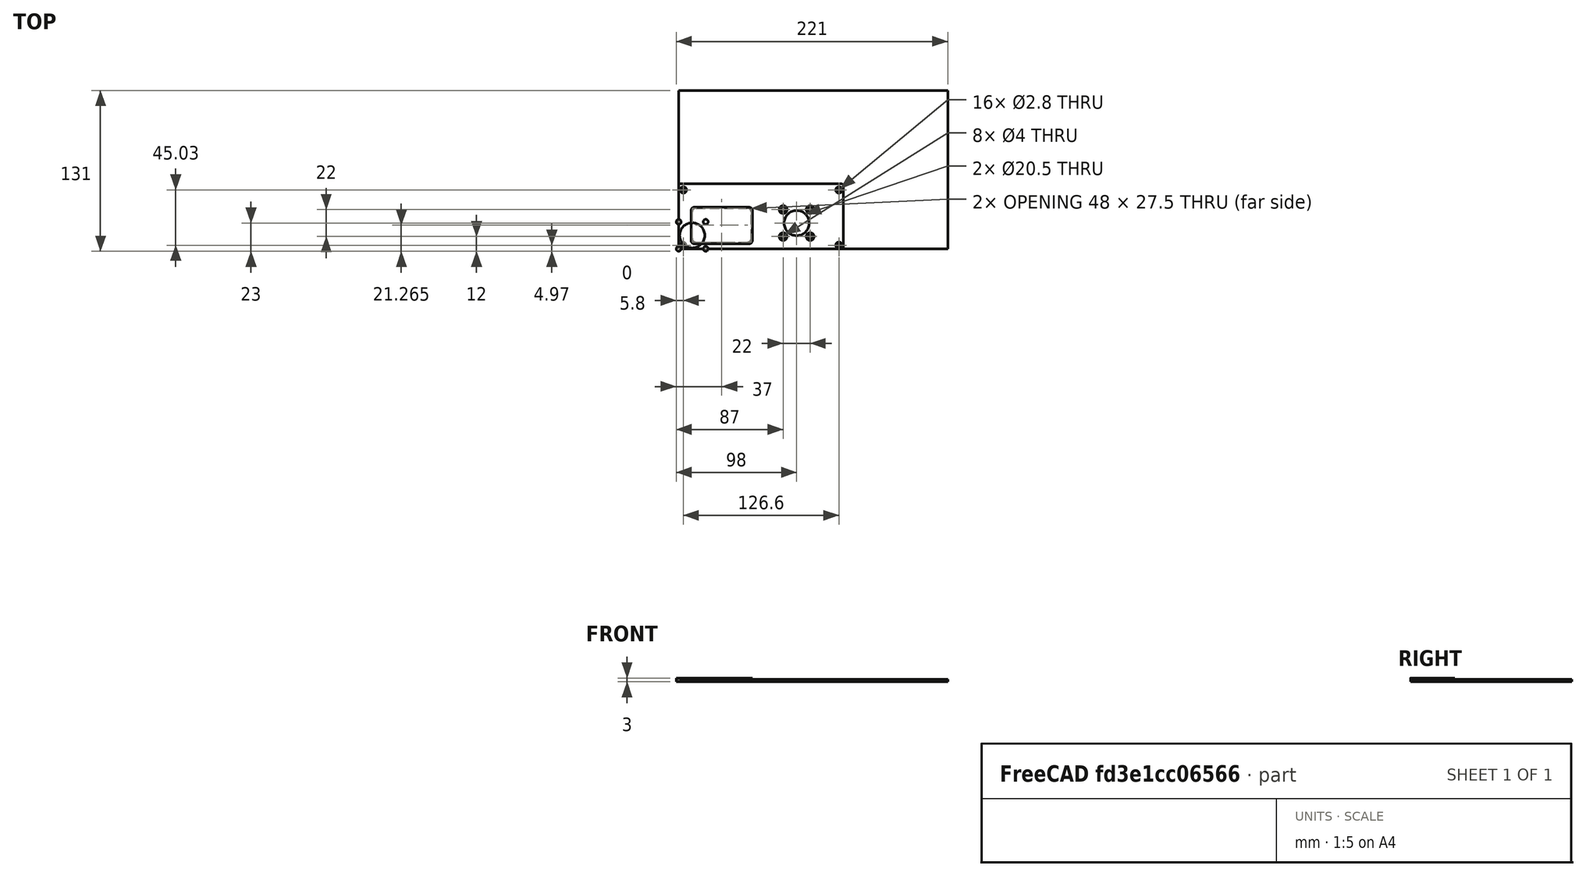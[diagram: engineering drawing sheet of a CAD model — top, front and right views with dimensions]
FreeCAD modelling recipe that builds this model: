
FCSTD DOCUMENT  (FreeCAD 0.17R13522 (Git))
Label: 温度控制器外壳dangyang
License: All rights reserved
LicenseURL: http://en.wikipedia.org/wiki/All_rights_reserved
objects: Drawing::FeatureViewPython×10, Part::Cylinder×6, Part::Feature×6, Part::Box×4, Part::Fillet×3, Part::Cut×3, Part::MultiFuse×2, Part::Chamfer×2, Part::FeaturePython×1, Raytracing::RayFeature×1, Raytracing::RayProject×1, Drawing::FeatureViewPart×1, Drawing::FeaturePage×1
note: 27 computed .brp shape members not serialized (recipe doc carries the construction recipe); baked Part::Feature solids carry a one-line shape summary decoded from their .brp

FEATURE [Part::Box] Box  label="立方体"
  AttacherType = Attacher::AttachEngine3D
  Height = 2
  Length = 134
  Width = 53
FEATURE [Part::Fillet] Fillet
  Base = -> Box
  Edges = 2 edges r=2: [Edge3,Edge7]
FEATURE [Part::Cylinder] Cylinder  label="圆柱体"
  Angle = 360
  AttacherType = Attacher::AttachEngine3D
  Height = 2
  Placement = pos=(3.8,2.97,0) rot=(0,0,1;0rad)
  Radius = 1.4
FEATURE [Part::Cylinder] Cylinder001  label="圆柱体001"
  Angle = 360
  AttacherType = Attacher::AttachEngine3D
  Height = 2
  Placement = pos=(3.8,48,0) rot=(0,0,1;0rad)
  Radius = 1.4
FEATURE [Part::Cylinder] Cylinder002  label="圆柱体002"
  Angle = 360
  AttacherType = Attacher::AttachEngine3D
  Height = 2
  Placement = pos=(130.4,2.97,0) rot=(0,0,1;0rad)
  Radius = 1.4
FEATURE [Part::Cylinder] Cylinder003  label="圆柱体003"
  Angle = 360
  AttacherType = Attacher::AttachEngine3D
  Height = 2
  Placement = pos=(130.4,48,0) rot=(0,0,1;0rad)
  Radius = 1.4
FEATURE [Part::MultiFuse] Fusion
  Shapes = -> [Cylinder,Cylinder003,Cylinder001,Cylinder002]
FEATURE [Part::Cut] Cut
  Base = -> Fillet
  Tool = -> Fusion
FEATURE [Part::Feature] Cut001
  shape: bbox 134 x 53 x 2 mm, 12 faces (baked)
FEATURE [Part::Chamfer] Chamfer
  Base = -> Cut001
  Edges = 4 edges r=1.2: [Edge10,Edge11,Edge12,Edge13]
FEATURE [Part::Box] Box001  label="立方体001"
  AttacherType = Attacher::AttachEngine3D
  Height = 2
  Length = 48
  Width = 27.5
FEATURE [Part::Fillet] Fillet001
  Base = -> Box001
  Edges = 4 edges r=3: [Edge1,Edge3,Edge5,Edge7]
  Placement = pos=(11,5.515,0) rot=(0,0,1;0rad)
FEATURE [Part::Box] Box002  label="立方体002"
  AttacherType = Attacher::AttachEngine3D
  Height = 3
  Length = 50
  Width = 30
FEATURE [Part::Fillet] Fillet002
  Base = -> Box002
  Edges = 4 edges r=3: [Edge1,Edge3,Edge5,Edge7]
  Placement = pos=(10,4,0) rot=(0,0,1;0rad)
FEATURE [Part::Cylinder] Cylinder004  label="圆柱体004"
  Angle = 360
  AttacherType = Attacher::AttachEngine3D
  Height = 3
  Radius = 2
FEATURE [Part::FeaturePython] Array  # Draft array (typed FeaturePython)
  Angle = 360
  ArrayType = 0
  Axis = (0,0,1)
  Base = -> Cylinder004
  Center = (0,0,0)
  Fuse = false
  IntervalAxis = (0,0,0)
  IntervalX = (22,0,0)
  IntervalY = (0,22,0)
  IntervalZ = (0,0,0)
  NumberPolar = 1
  NumberX = 2
  NumberY = 2
  NumberZ = 1
FEATURE [Part::Cylinder] Cylinder005  label="圆柱体005"
  Angle = 360
  AttacherType = Attacher::AttachEngine3D
  Height = 3
  Placement = pos=(11,11,0) rot=(0,0,1;0rad)
  Radius = 10.25
FEATURE [Part::MultiFuse] Fusion001
  Shapes = -> [Cylinder005,Array]
FEATURE [Part::Feature] Fusion001001  label="Fusion002"
  Placement = pos=(85,10,0) rot=(0,0,1;0rad)
  shape: bbox 26 x 26 x 3 mm, 15 faces, 5 solids (baked)
FEATURE [Part::Feature] Fillet001001  label="Fillet003"
  Placement = pos=(11,5.515,0) rot=(0,0,1;0rad)
  shape: bbox 48 x 27.5 x 2 mm, 10 faces (baked)
FEATURE [Part::Feature] Chamfer001
  shape: bbox 134 x 53 x 2 mm, 16 faces (baked)
FEATURE [Part::Cut] Cut002
  Base = -> Chamfer001
  Tool = -> Fillet001001
FEATURE [Part::Cut] Cut003
  Base = -> Cut002
  Tool = -> Fusion001001
FEATURE [Part::Feature] Cut003001  label="Cut004"
  shape: bbox 134 x 53 x 2 mm, 29 faces (baked)
FEATURE [Part::Chamfer] Chamfer002
  Base = -> Cut003001
  Edges = 4 edges r=1.2: [Edge15,Edge16,Edge17,Edge19]
FEATURE [Part::Feature] Chamfer002001  label="Chamfer003"
  shape: bbox 134 x 53 x 2 mm, 33 faces (baked)
FEATURE [Raytracing::RayFeature] Chamfer002001_View
  Result = <blob: 234618 chars omitted>
  Source = -> Chamfer002001
  Transparency = 0
FEATURE [Raytracing::RayProject] PovProject
  Camera = // declares position and view direction\n\n// Generated by FreeCAD (http://www.freecadweb.org/)\n#declare cam_location =  <127.48,63.3881,-66.5857>;\n#declare cam_look_at  = <66.5399,2.44758,-5.64513>;\n#declare cam_sky      = <-0.408248,0.816497,0.408248>;\n#declare cam_angle    = 45; \ncamera {\n  location  cam_location\n  look_at   cam_look_at\n  sky       cam_sky\n  angle     cam_angle \n  right x*800/600\n}
  Group = -> [Chamfer002001_View]
  Template = <path>
FEATURE [Drawing::FeatureViewPart] Ortho  label="Ortho_0_0"
  Direction = (0,0,1)
  HiddenWidth = 0.15
  LineWidth = 0.35
  Rotation = 0
  ShowHiddenLines = false
  ShowSmoothLines = false
  Source = -> Chamfer002001
  Tolerance = 0.05
  ViewResult = <g id="Ortho_0_0"\n   transform="rotate(0,48,125.75) translate(48,125.75) scale(1,1)"\n  >\n<g   fill="none"\n   stroke="rgb(0, 0, 0)"\n   stroke-linecap="butt"\n   stroke-linejoin="miter"\n   stroke-width="0.350000"\n   transform="scale(1,-1)"\n  >\n<circle cx ="85" cy ="10" r ="3.2" /><path id= "2" d=" M 0 0 L 0 51 " />\n<path d="M-4.44089e-16 51 A2 2 0 0 0 2 53" /><path id= "4" d=" M 0 0 L 134 0 " />\n<path id= "5" d=" M 2 53 L 132 53 " />\n<path id= "6" d=" M 134 0 L 134 51 " />\n<path d="M134 51 A2 2 0 0 1 132 53" /><path d="M11 8.515 A3 3 0 0 1 14 5.515" /><path id= "9" d=" M 11 8.515 L 11 30.015 " />\n<path id= "10" d=" M 14 5.515 L 56 5.515 " />\n<path d="M11 30.015 A3 3 0 0 0 14 33.015" /><path d="M59 8.515 A3 3 0 0 0 56 5.515" /><path id= "13" d=" M 14 33.015 L 56 33.015 " />\n<path id= "14" d=" M 59 8.515 L 59 30.015 " />\n<path d="M59 30.015 A3 3 0 0 1 56 33.015" /><circle cx ="96" cy ="21" r ="10.25" /><circle cx ="3.8" cy ="2.97" r ="2.6" /><circle cx ="130.4" cy ="2.97" r ="2.6" /><circle cx ="3.8" cy ="48" r ="2.6" /><circle cx ="130.4" cy ="48" r ="2.6" /><circle cx ="85" cy ="32" r ="3.2" /><circle cx ="107" cy ="10" r ="3.2" /><circle cx ="107" cy ="32" r ="3.2" /><circle cx ="85" cy ="10" r ="2" /><circle cx ="3.8" cy ="2.97" r ="1.4" /><circle cx ="130.4" cy ="2.97" r ="1.4" /><circle cx ="3.8" cy ="48" r ="1.4" /><circle cx ="130.4" cy ="48" r ="1.4" /><circle cx ="85" cy ="32" r ="2" /><circle cx ="107" cy ="10" r ="2" /><circle cx ="107" cy ="32" r ="2" /></g>\n</g>
  Visible = false
  X = 48
  Y = 125.75
FEATURE [Drawing::FeatureViewPython] centerLines001  # drawing view (typed FeaturePython)
  Rotation = 0
  ViewResult = <g transform="scale(1.000000,1.000000)" stroke="rgb(0,0,255)"  stroke-width="0.320000" > <path d="M 144.000000,104.750000 L 144.000000,107.750000 M 144.000000,109.750000 L 144.000000,115.750000 M 144.000000,117.750000 L 144.000000,120.750000 M 144.000000,122.750000 L 144.000000,124.245155 "/>\n<path d="M 144.000000,104.750000 L 141.000000,104.750000 M 139.000000,104.750000 L 133.000000,104.750000 M 131.000000,104.750000 L 128.000000,104.750000 M 126.000000,104.750000 L 123.781554,104.750000 "/>\n<path d="M 144.000000,104.750000 L 144.000000,107.750000 M 144.000000,109.750000 L 144.000000,115.750000 "/>\n<path d="M 144.000000,104.750000 L 141.000000,104.750000 M 139.000000,104.750000 L 133.000000,104.750000 M 131.000000,104.750000 L 128.000000,104.750000 M 126.000000,104.750000 L 125.326891,104.750000 "/> </g> 
  Visible = false
  X = 0
  Y = 0
  centerLine_color = rgb(0,0,255)
  centerLine_len_dash = 6
  centerLine_len_dot = 3
  centerLine_len_gap = 2
  centerLine_width = 0.32
  click1_x = 123.782
  click1_y = 124.245
  click2_x = 125.327
  click2_y = 116.518
FEATURE [Drawing::FeatureViewPython] centerLines002  # drawing view (typed FeaturePython)
  Rotation = 0
  ViewResult = <g transform="scale(1.000000,1.000000)" stroke="rgb(0,0,255)"  stroke-width="0.320000" > <path d="M 144.000000,104.750000 L 144.000000,101.750000 M 144.000000,99.750000 L 144.000000,93.750000 M 144.000000,91.750000 L 144.000000,88.750000 "/>\n<path d="M 144.000000,104.750000 L 147.000000,104.750000 M 149.000000,104.750000 L 155.000000,104.750000 M 157.000000,104.750000 L 160.000000,104.750000 M 162.000000,104.750000 L 162.724065,104.750000 "/>\n<path d="M 144.000000,104.750000 L 144.000000,101.750000 M 144.000000,99.750000 L 144.000000,93.750000 "/>\n<path d="M 144.000000,104.750000 L 144.334546,104.750000 "/> </g> 
  Visible = false
  X = 0
  Y = 0
  centerLine_color = rgb(0,0,255)
  centerLine_len_dash = 6
  centerLine_len_dot = 3
  centerLine_len_gap = 2
  centerLine_width = 0.32
  click1_x = 162.724
  click1_y = 87.4661
  click2_x = 144.335
  click2_y = 92.5657
FEATURE [Drawing::FeatureViewPython] centerLines003  # drawing view (typed FeaturePython)
  Rotation = 0
  ViewResult = <g transform="scale(1.000000,1.000000)" stroke="rgb(0,0,255)"  stroke-width="0.320000" > <path d="M 133.000000,93.750000 L 133.000000,90.750000 M 133.000000,88.750000 L 133.000000,84.409222 "/>\n<path d="M 133.000000,93.750000 L 130.000000,93.750000 M 128.000000,93.750000 L 122.913490,93.750000 "/>\n<path d="M 133.000000,93.750000 L 133.000000,96.750000 M 133.000000,98.750000 L 133.000000,102.108765 "/>\n<path d="M 133.000000,93.750000 L 136.000000,93.750000 M 138.000000,93.750000 L 141.130563,93.750000 "/> </g> 
  Visible = false
  X = 0
  Y = 0
  centerLine_color = rgb(0,0,255)
  centerLine_len_dash = 6
  centerLine_len_dot = 3
  centerLine_len_gap = 2
  centerLine_width = 0.32
  click1_x = 122.913
  click1_y = 84.4092
  click2_x = 141.131
  click2_y = 102.109
FEATURE [Drawing::FeatureViewPython] centerLines004  # drawing view (typed FeaturePython)
  Rotation = 0
  ViewResult = <g transform="scale(1.000000,1.000000)" stroke="rgb(0,0,255)"  stroke-width="0.320000" > <path d="M 155.000000,93.750000 L 155.000000,90.750000 M 155.000000,88.750000 L 155.000000,83.276534 "/>\n<path d="M 155.000000,93.750000 L 158.000000,93.750000 M 160.000000,93.750000 L 166.000000,93.750000 "/>\n<path d="M 155.000000,93.750000 L 155.000000,96.750000 M 155.000000,98.750000 L 155.000000,102.915201 "/>\n<path d="M 155.000000,93.750000 L 152.000000,93.750000 M 150.000000,93.750000 L 146.807086,93.750000 "/> </g> 
  Visible = false
  X = 0
  Y = 0
  centerLine_color = rgb(0,0,255)
  centerLine_len_dash = 6
  centerLine_len_dot = 3
  centerLine_len_gap = 2
  centerLine_width = 0.32
  click1_x = 167.412
  click1_y = 83.2765
  click2_x = 146.807
  click2_y = 102.915
FEATURE [Drawing::FeatureViewPython] centerLines005  # drawing view (typed FeaturePython)
  Rotation = 0
  ViewResult = <g transform="scale(1.000000,1.000000)" stroke="rgb(0,0,255)"  stroke-width="0.320000" > <path d="M 133.000000,115.750000 L 133.000000,112.750000 M 133.000000,110.750000 L 133.000000,107.422436 "/>\n<path d="M 133.000000,115.750000 L 130.000000,115.750000 M 128.000000,115.750000 L 123.841650,115.750000 "/>\n<path d="M 133.000000,115.750000 L 133.000000,118.750000 M 133.000000,120.750000 L 133.000000,123.519705 "/>\n<path d="M 133.000000,115.750000 L 136.000000,115.750000 M 138.000000,115.750000 L 142.192536,115.750000 "/> </g> 
  Visible = false
  X = 0
  Y = 0
  centerLine_color = rgb(0,0,255)
  centerLine_len_dash = 6
  centerLine_len_dot = 3
  centerLine_len_gap = 2
  centerLine_width = 0.32
  click1_x = 123.842
  click1_y = 107.422
  click2_x = 142.193
  click2_y = 123.52
FEATURE [Drawing::FeatureViewPython] centerLines006  # drawing view (typed FeaturePython)
  Rotation = 0
  ViewResult = <g transform="scale(1.000000,1.000000)" stroke="rgb(0,0,255)"  stroke-width="0.320000" > <path d="M 155.000000,115.750000 L 155.000000,112.750000 M 155.000000,110.750000 L 155.000000,108.280957 "/>\n<path d="M 155.000000,115.750000 L 152.000000,115.750000 M 150.000000,115.750000 L 147.558292,115.750000 "/>\n<path d="M 155.000000,115.750000 L 155.000000,118.750000 M 155.000000,120.750000 L 155.000000,124.163595 "/>\n<path d="M 155.000000,115.750000 L 158.000000,115.750000 M 160.000000,115.750000 L 165.265287,115.750000 "/> </g> 
  Visible = false
  X = 0
  Y = 0
  centerLine_color = rgb(0,0,255)
  centerLine_len_dash = 6
  centerLine_len_dot = 3
  centerLine_len_gap = 2
  centerLine_width = 0.32
  click1_x = 147.558
  click1_y = 108.281
  click2_x = 165.265
  click2_y = 124.164
FEATURE [Drawing::FeatureViewPython] centerLines007  # drawing view (typed FeaturePython)
  Rotation = 0
  ViewResult = <g transform="scale(1.000000,1.000000)" stroke="rgb(0,0,255)"  stroke-width="0.320000" > <path d="M 62.000000,95.735000 L 62.000000,92.735000 M 62.000000,90.735000 L 62.000000,87.266132 "/>\n<path d="M 62.000000,95.735000 L 59.000000,95.735000 M 57.000000,95.735000 L 54.995843,95.735000 "/>\n<path d="M 62.000000,95.735000 L 62.000000,98.735000 M 62.000000,100.735000 L 62.000000,106.735000 M 62.000000,108.735000 L 62.000000,111.735000 M 62.000000,113.735000 L 62.000000,119.735000 M 62.000000,121.735000 L 62.000000,124.263335 "/>\n<path d="M 62.000000,95.735000 L 65.000000,95.735000 M 67.000000,95.735000 L 73.000000,95.735000 M 75.000000,95.735000 L 78.000000,95.735000 M 80.000000,95.735000 L 86.000000,95.735000 M 88.000000,95.735000 L 91.000000,95.735000 M 93.000000,95.735000 L 99.000000,95.735000 M 101.000000,95.735000 L 104.000000,95.735000 M 106.000000,95.735000 L 112.000000,95.735000 "/> </g> 
  Visible = false
  X = 0
  Y = 0
  centerLine_color = rgb(0,0,255)
  centerLine_len_dash = 6
  centerLine_len_dot = 3
  centerLine_len_gap = 2
  centerLine_width = 0.32
  click1_x = 54.9958
  click1_y = 87.2661
  click2_x = 113.628
  click2_y = 124.263
FEATURE [Drawing::FeatureViewPython] centerLines008  # drawing view (typed FeaturePython)
  Rotation = 0
  ViewResult = <g transform="scale(1.000000,1.000000)" stroke="rgb(0,0,255)"  stroke-width="0.320000" > <path d="M 104.000000,95.735000 L 104.000000,92.735000 M 104.000000,90.735000 L 104.000000,87.720643 "/>\n<path d="M 104.000000,95.735000 L 107.000000,95.735000 "/>\n<path d="M 104.000000,95.735000 L 104.000000,98.735000 M 104.000000,100.735000 L 104.000000,106.735000 M 104.000000,108.735000 L 104.000000,111.735000 M 104.000000,113.735000 L 104.000000,119.735000 M 104.000000,121.735000 L 104.000000,122.627095 "/>\n<path d="M 104.000000,95.735000 L 101.000000,95.735000 M 99.000000,95.735000 L 93.000000,95.735000 M 91.000000,95.735000 L 90.265905,95.735000 "/> </g> 
  Visible = false
  X = 0
  Y = 0
  centerLine_color = rgb(0,0,255)
  centerLine_len_dash = 6
  centerLine_len_dot = 3
  centerLine_len_gap = 2
  centerLine_width = 0.32
  click1_x = 108.992
  click1_y = 87.7206
  click2_x = 90.2659
  click2_y = 122.627
FEATURE [Drawing::FeatureViewPython] centerLines009  # drawing view (typed FeaturePython)
  Rotation = 0
  ViewResult = <g transform="scale(1.000000,1.000000)" stroke="rgb(0,0,255)"  stroke-width="0.320000" > <path d="M 62.000000,117.235000 L 62.000000,120.235000 M 62.000000,122.235000 L 62.000000,124.172433 "/>\n<path d="M 62.000000,117.235000 L 59.000000,117.235000 M 57.000000,117.235000 L 54.632234,117.235000 "/>\n<path d="M 62.000000,117.235000 L 62.000000,118.536495 "/>\n<path d="M 62.000000,117.235000 L 65.000000,117.235000 M 67.000000,117.235000 L 73.000000,117.235000 M 75.000000,117.235000 L 78.000000,117.235000 M 80.000000,117.235000 L 86.000000,117.235000 M 88.000000,117.235000 L 91.000000,117.235000 M 93.000000,117.235000 L 99.000000,117.235000 M 101.000000,117.235000 L 104.000000,117.235000 M 106.000000,117.235000 L 112.000000,117.235000 "/> </g> 
  Visible = false
  X = 0
  Y = 0
  centerLine_color = rgb(0,0,255)
  centerLine_len_dash = 6
  centerLine_len_dot = 3
  centerLine_len_gap = 2
  centerLine_width = 0.32
  click1_x = 54.6322
  click1_y = 124.172
  click2_x = 112.901
  click2_y = 118.536
FEATURE [Drawing::FeatureViewPython] centerLines010  # drawing view (typed FeaturePython)
  Rotation = 0
  ViewResult = <g transform="scale(1.000000,1.000000)" stroke="rgb(0,0,255)"  stroke-width="0.320000" > <path d="M 104.000000,117.235000 L 104.000000,114.235000 M 104.000000,112.235000 L 104.000000,107.355522 "/>\n<path d="M 104.000000,117.235000 L 101.000000,117.235000 "/>\n<path d="M 104.000000,117.235000 L 104.000000,120.235000 M 104.000000,122.235000 L 104.000000,125.354162 "/>\n<path d="M 104.000000,117.235000 L 107.000000,117.235000 M 109.000000,117.235000 L 110.991611,117.235000 "/> </g> 
  Visible = false
  X = 0
  Y = 0
  centerLine_color = rgb(0,0,255)
  centerLine_len_dash = 6
  centerLine_len_dot = 3
  centerLine_len_gap = 2
  centerLine_width = 0.32
  click1_x = 99.447
  click1_y = 107.356
  click2_x = 110.992
  click2_y = 125.354
FEATURE [Drawing::FeaturePage] Page
  EditableTexts = AUTHOR NAME | DRAWING TITLE | FreeCAD DRAWING | A4 | X / Y | SCALE | PN | DN | DD/MM/YYYY | REV A
  Group = -> [Ortho,centerLines001,centerLines002,centerLines003,centerLines004,centerLines005,centerLines006,centerLines007,centerLines008,centerLines009,centerLines010]
  Template = <path>
FEATURE [Part::Box] Box003  label="立方体003"
  AttacherType = Attacher::AttachEngine3D
  Height = 2
  Length = 219
  Width = 129
note: 2 file-system paths scrubbed to <path> (originals preserved in the JSON sidecar)
